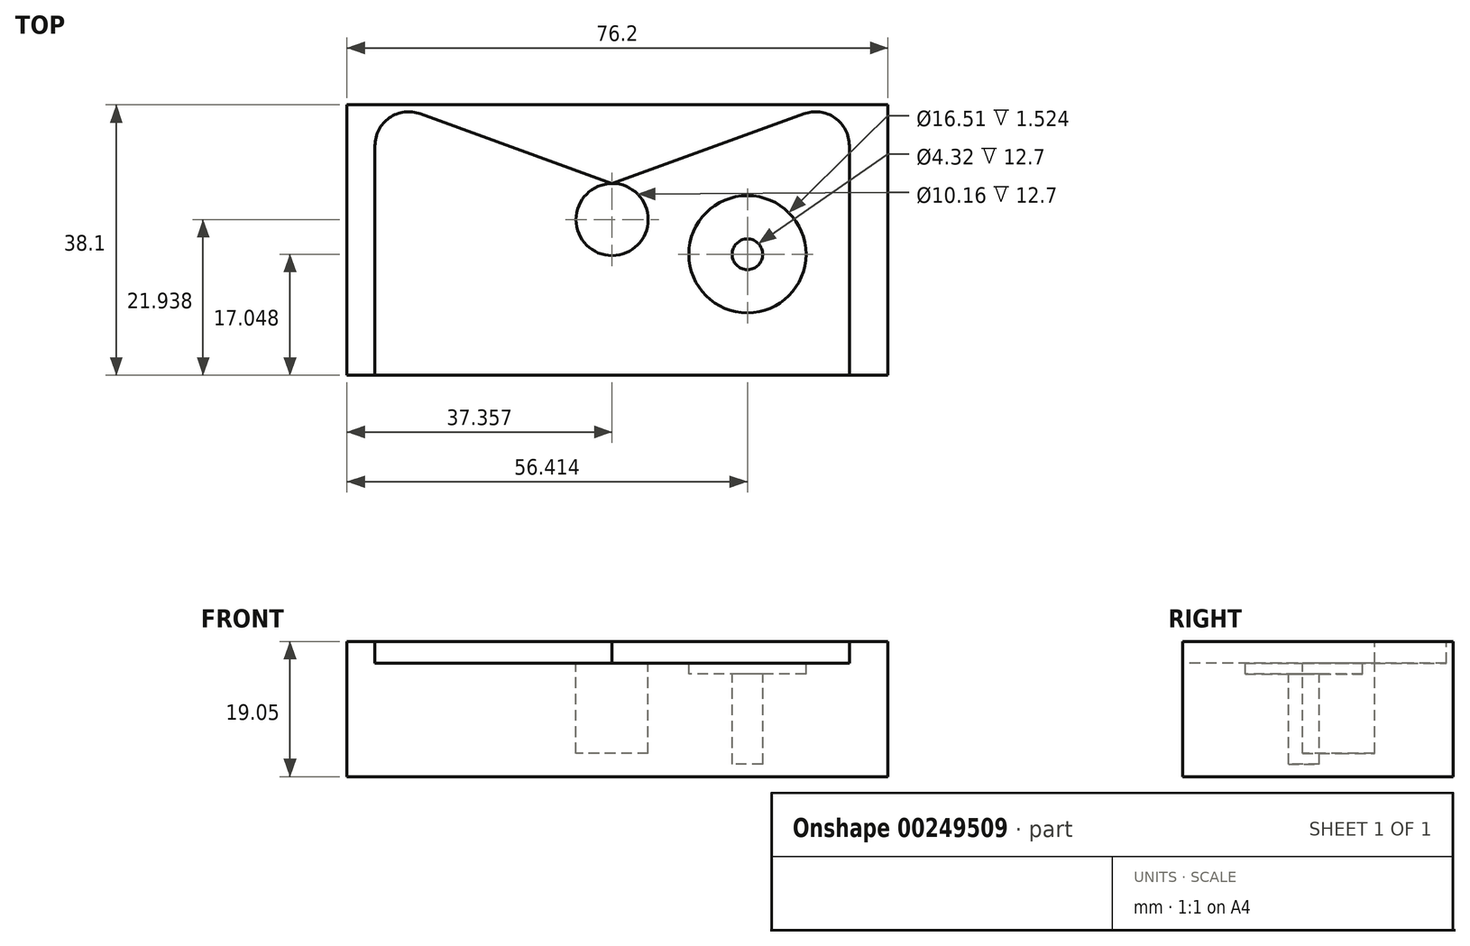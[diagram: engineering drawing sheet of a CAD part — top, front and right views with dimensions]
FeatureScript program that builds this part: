
annotation { "Feature Type Name" : "Feature", "Feature Type Description" : "" }
export const myFeature = defineFeature(function(context is Context, id is Id, definition is map)
    precondition{}
    {
        {
            var Q0;
            Q0=qCreatedBy(makeId("Top.planeOp"),FACE);
            var sketch = newSketch(context, id + "F0", { "sketchPlane" : qUnion([Q0])});
            skLineSegment(sketch, "E0.bottom", {"start": v(0, 0) * mm, "end": v(76.2, 0) * mm});
            skLineSegment(sketch, "E0.top", {"start": v(0, 38.1) * mm, "end": v(76.2, 38.1) * mm});
            skLineSegment(sketch, "E0.left", {"start": v(0, 0) * mm, "end": v(0, 38.1) * mm});
            skLineSegment(sketch, "E0.right", {"start": v(76.2, 0) * mm, "end": v(76.2, 38.1) * mm});
            skCircle(sketch, "E1", {"center": v(-28.07, -40.86) * mm, "radius": 4.76 * mm, "construction": true});
            skCircle(sketch, "E2", {"center": v(-0.1, -28.76) * mm, "radius": 4.76 * mm, "construction": true});
            skCircle(sketch, "E3", {"center": v(29.11, -37.47) * mm, "radius": 4.76 * mm, "construction": true});
            skLineSegment(sketch, "E4", {"start": v(-28.07, -40.86) * mm, "end": v(-0.1, -28.76) * mm, "construction": true});
            skLineSegment(sketch, "E5", {"start": v(-0.1, -28.76) * mm, "end": v(29.11, -37.47) * mm, "construction": true});
            skSolve(sketch);
        }
        {
            var Q0;
            Q0 = qSketchRegion(id + "F0", true);
            extrude(context, id + "F1", {"entities" : qUnion([Q0]), "depth" : 19.05 * mm});
        }
        {
            var Q0;
            Q0=makeQuery(id+"F1.opExtrude","CAP_FACE",FACE,{"disambiguationData":[OSD([sQuery(id+"F0.wireOp",EDGE,"E0.bottom"),sQuery(id+"F0.wireOp",EDGE,"E0.top"),sQuery(id+"F0.wireOp",EDGE,"E0.left"),sQuery(id+"F0.wireOp",EDGE,"E0.right")])],"isStart":false});
            var sketch = newSketch(context, id + "F2", { "sketchPlane" : qUnion([Q0])});
            skCircle(sketch, "E6", {"center": v(8.72, 32.36) * mm, "radius": 4.76 * mm});
            skCircle(sketch, "E7", {"center": v(37.36, 21.94) * mm, "radius": 4.76 * mm});
            skCircle(sketch, "E8", {"center": v(66, 32.36) * mm, "radius": 4.76 * mm});
            skLineSegment(sketch, "E9", {"start": v(8.72, 32.36) * mm, "end": v(37.36, 21.94) * mm, "construction": true});
            skLineSegment(sketch, "E10", {"start": v(37.36, 21.94) * mm, "end": v(66, 32.36) * mm, "construction": true});
            skLineSegment(sketch, "E11", {"start": v(7.09, 27.89) * mm, "end": v(35.73, 17.46) * mm});
            skLineSegment(sketch, "E12", {"start": v(38.99, 26.41) * mm, "end": v(10.34, 36.84) * mm});
            skLineSegment(sketch, "E13", {"start": v(35.73, 26.41) * mm, "end": v(64.37, 36.84) * mm});
            skLineSegment(sketch, "E14", {"start": v(67.63, 27.89) * mm, "end": v(38.99, 17.46) * mm});
            skSolve(sketch);
        }
        {
            var Q0;
            Q0 = qSketchRegion(id + "F2", true);
            extrude(context, id + "F3", {"entities" : qUnion([Q0]), "operationType" : NewBodyOperationType.REMOVE, "oppositeDirection" : true, "depth" : 3.05 * mm});
        }
        {
            var Q0;
            Q0=makeQuery(id+"F1.opExtrude","CAP_FACE",FACE,{"disambiguationData":[OSD([sQuery(id+"F0.wireOp",EDGE,"E0.bottom"),sQuery(id+"F0.wireOp",EDGE,"E0.top"),sQuery(id+"F0.wireOp",EDGE,"E0.left"),sQuery(id+"F0.wireOp",EDGE,"E0.right")])],"isStart":false});
            var sketch = newSketch(context, id + "F4", { "sketchPlane" : qUnion([Q0])});
            skCircle(sketch, "E15", {"center": v(56.41, 17.05) * mm, "radius": 8.26 * mm});
            skSolve(sketch);
        }
        {
            var Q0;
            Q0 = qSketchRegion(id + "F4", true);
            extrude(context, id + "F5", {"entities" : qUnion([Q0]), "operationType" : NewBodyOperationType.REMOVE, "oppositeDirection" : true, "depth" : 4.57 * mm});
        }
        {
            var Q0;
            Q0=makeQuery(id+"F5.boolean.opBoolean","COPY",FACE,{"derivedFrom":makeQuery(id+"F5.opExtrude","CAP_FACE",FACE,{"disambiguationData":[OSD([sQuery(id+"F4.wireOp",EDGE,"E15")])],"isStart":false})});
            var sketch = newSketch(context, id + "F6", { "sketchPlane" : qUnion([Q0])});
            skCircle(sketch, "E16", {"center": v(56.41, 17.05) * mm, "radius": 2.16 * mm});
            skSolve(sketch);
        }
        {
            var Q0;
            Q0 = qSketchRegion(id + "F6", true);
            extrude(context, id + "F7", {"entities" : qUnion([Q0]), "operationType" : NewBodyOperationType.REMOVE, "oppositeDirection" : true, "depth" : 12.7 * mm});
        }
        {
            var Q0;
            Q0=makeQuery(id+"F3.boolean.opBoolean","COPY",FACE,{"derivedFrom":makeQuery(id+"F3.opExtrude","CAP_FACE",FACE,{"disambiguationData":[OSD([sQuery(id+"F2.wireOp",EDGE,"E6"),sQuery(id+"F2.wireOp",EDGE,"E7"),sQuery(id+"F2.wireOp",EDGE,"E8"),sQuery(id+"F2.wireOp",EDGE,"E11"),sQuery(id+"F2.wireOp",EDGE,"E12"),sQuery(id+"F2.wireOp",EDGE,"E13"),sQuery(id+"F2.wireOp",EDGE,"E14")])],"isStart":false})});
            var sketch = newSketch(context, id + "F8", { "sketchPlane" : qUnion([Q0])});
            skCircle(sketch, "E17", {"center": v(37.36, 21.94) * mm, "radius": 5.08 * mm});
            skSolve(sketch);
        }
        {
            var Q0;
            Q0 = qSketchRegion(id + "F8", true);
            extrude(context, id + "F9", {"entities" : qUnion([Q0]), "operationType" : NewBodyOperationType.REMOVE, "oppositeDirection" : true, "depth" : 12.7 * mm});
        }
        {
            var Q0;
            Q0=makeQuery(id+"F1.opExtrude","CAP_FACE",FACE,{"disambiguationData":[OSD([sQuery(id+"F0.wireOp",EDGE,"E0.bottom"),sQuery(id+"F0.wireOp",EDGE,"E0.top"),sQuery(id+"F0.wireOp",EDGE,"E0.left"),sQuery(id+"F0.wireOp",EDGE,"E0.right")])],"isStart":false});
            var sketch = newSketch(context, id + "F10", { "sketchPlane" : qUnion([Q0])});
            skLineSegment(sketch, "E18", {"start": v(3.95, 32.36) * mm, "end": v(3.95, 0) * mm});
            skLineSegment(sketch, "E19", {"start": v(3.95, 0) * mm, "end": v(70.76, 0) * mm});
            skLineSegment(sketch, "E20", {"start": v(70.76, 0) * mm, "end": v(70.76, 32.36) * mm});
            skArc(sketch, "E21.0", {"start": v(7.09, 27.89) * mm, "mid": v(4.81, 29.63) * mm, "end": v(3.95, 32.36) * mm});
            skLineSegment(sketch, "E22.0", {"start": v(7.09, 27.89) * mm, "end": v(35.73, 17.46) * mm});
            skArc(sketch, "E23.0", {"start": v(38.99, 17.46) * mm, "mid": v(37.36, 17.18) * mm, "end": v(35.73, 17.46) * mm});
            skLineSegment(sketch, "E24.0", {"start": v(49.29, 21.21) * mm, "end": v(38.99, 17.46) * mm});
            skPoint(sketch, "E25.0", {"position": v(63.41, 26.35) * mm});
            skLineSegment(sketch, "E26.0", {"start": v(67.63, 27.89) * mm, "end": v(59.2, 24.82) * mm});
            skArc(sketch, "E27.0", {"start": v(67.63, 27.89) * mm, "mid": v(69.9, 29.63) * mm, "end": v(70.76, 32.36) * mm});
            skLineSegment(sketch, "E28", {"start": v(49.29, 21.21) * mm, "end": v(59.2, 24.82) * mm});
            skPoint(sketch, "E29.orphan", {"position": v(10.34, 36.84) * mm});
            skPoint(sketch, "E30.orphan", {"position": v(64.37, 36.84) * mm});
            skSolve(sketch);
        }
        {
            var Q0;
            Q0 = qSketchRegion(id + "F10", true);
            extrude(context, id + "F11", {"entities" : qUnion([Q0]), "operationType" : NewBodyOperationType.REMOVE, "oppositeDirection" : true, "depth" : 3.05 * mm});
        }
    });
